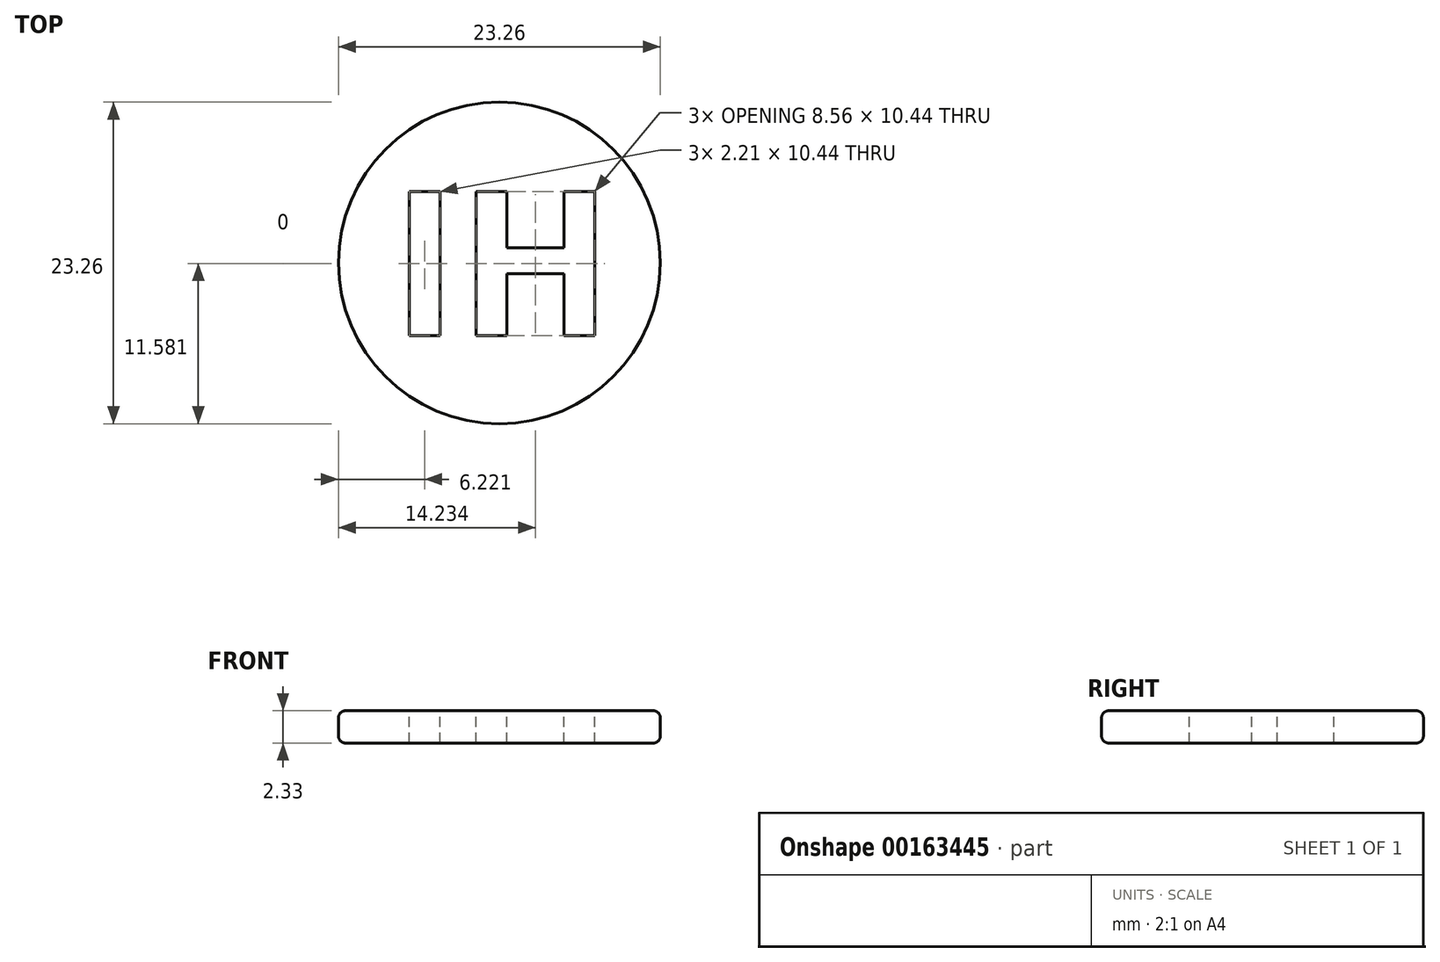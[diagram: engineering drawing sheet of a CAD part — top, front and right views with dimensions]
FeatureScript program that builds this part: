
annotation { "Feature Type Name" : "Feature", "Feature Type Description" : "" }
export const myFeature = defineFeature(function(context is Context, id is Id, definition is map)
    precondition{}
    {
        {
            var Q0;
            Q0=qCreatedBy(makeId("Top.planeOp"),FACE);
            var sketch = newSketch(context, id + "F0", { "sketchPlane" : qUnion([Q0])});
            skCircle(sketch, "E0", {"center": v(0, 0) * mm, "radius": 11.62 * mm});
            skSolve(sketch);
        }
        {
            var Q0;
            Q0 = qSketchRegion(id + "F0", true);
            extrude(context, id + "F1", {"entities" : qUnion([Q0]), "depth" : 2.33 * mm});
        }
        {
            var Q0;
            Q0=makeQuery(id+"F1.opExtrude","CAP_FACE",FACE,{"disambiguationData":[OSD([sQuery(id+"F0.wireOp",EDGE,"E0")])],"isStart":false});
            var sketch = newSketch(context, id + "F2", { "sketchPlane" : qUnion([Q0])});
            skText(sketch, "E1", { "text": "IH", "fontName": "OpenSans-Bold.ttf"});
            const initialGuessF2  = {"E1": [-0.00783, -0.00527, 1, 0, 0.01053]};
            skSetInitialGuess(sketch, initialGuessF2);
            skSolve(sketch);
        }
        {
            var Q0;
            Q0 = qSketchRegion(id + "F2", true);
            extrude(context, id + "F3", {"entities" : qUnion([Q0]), "operationType" : NewBodyOperationType.REMOVE, "endBound" : BoundingType.THROUGH_ALL, "oppositeDirection" : true, "depth" : 25 * mm});
        }
        {
            var Q0;
            Q0=makeQuery(id+"F1.opExtrude","CAP_EDGE",EDGE,{"disambiguationData":[OSD([sQuery(id+"F0.wireOp",EDGE,"E0")])],"isStart":false});
            var Q1;
            Q1=makeQuery(id+"F1.opExtrude","CAP_EDGE",EDGE,{"disambiguationData":[OSD([sQuery(id+"F0.wireOp",EDGE,"E0")])],"isStart":true});
            fillet(context, id + "F4", {"entities" : qUnion([Q0, Q1]), "radius" : 0.5 * mm, "tangentPropagation" : true, "allowEdgeOverflow" : false});
        }
    });
